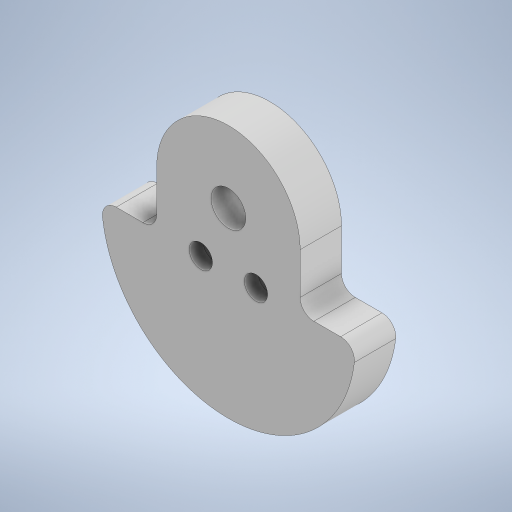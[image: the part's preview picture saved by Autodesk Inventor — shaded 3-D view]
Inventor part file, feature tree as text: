
AUTODESK INVENTOR PART (.ipt)
format: ipt  version: 2023 (Build 270158000, 158)  size: 480,768 bytes
history: native  units: in
note: dims shown in document units (in); Inventor stores cm internally (conversion verified against a paired STEP export)
features: extrude x5, sketch x1, fillet x1
ambient origin geometry x8: Origin, YZ Plane, XZ Plane, XY Plane, X Axis, Y Axis, Z Axis, Center Point
bodies: Body1 (feature_tree)
feature tree (7):
  sketch  "Sketch1"  dims[d3=0.866in d15=0.75in d20=0.314in d37=0.75in d44=0.125in d51=0.21in d52=0.21in d57=0.512in d58=0.5in d59=0.0in d60=0.125in d61=0.0in d62=1.5in d63=0.0in d64=1.5in d65=0.0in d66=0.375in d67=0.0in d68=0.125in]
  extrude  "Extrusion9"  Depth=0.125in
  extrude  "Extrusion10"  Depth=0.125in
  extrude  "Extrusion11"  Depth=0.125in
  extrude  "Extrusion12"  Depth=0.125in
  extrude  "Extrusion13"  Depth=0.125in
  fillet  "Fillet2"  Radius=0.512in
